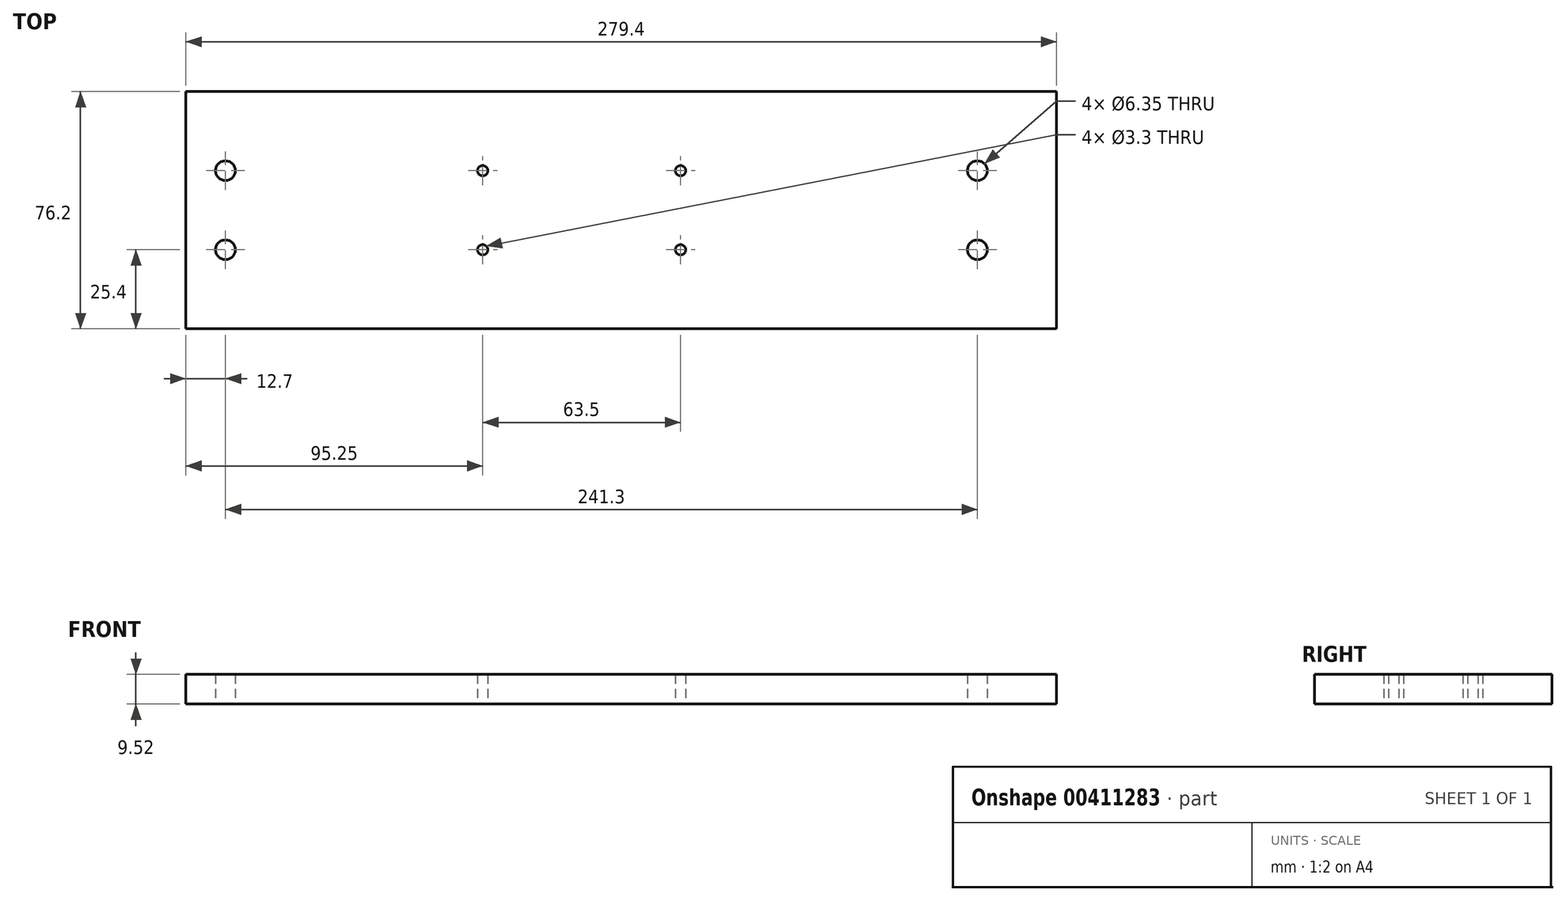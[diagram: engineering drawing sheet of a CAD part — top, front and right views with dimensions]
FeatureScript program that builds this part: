
annotation { "Feature Type Name" : "Feature", "Feature Type Description" : "" }
export const myFeature = defineFeature(function(context is Context, id is Id, definition is map)
    precondition{}
    {
        {
            var Q0;
            Q0=qCreatedBy(makeId("Top.planeOp"),FACE);
            var sketch = newSketch(context, id + "F0", { "sketchPlane" : qUnion([Q0])});
            skLineSegment(sketch, "E0.bottom", {"start": v(-152.4, 38.1) * mm, "end": v(127, 38.1) * mm});
            skLineSegment(sketch, "E0.top", {"start": v(-152.4, -38.1) * mm, "end": v(127, -38.1) * mm});
            skLineSegment(sketch, "E0.left", {"start": v(-152.4, 38.1) * mm, "end": v(-152.4, -38.1) * mm});
            skLineSegment(sketch, "E0.right", {"start": v(127, 38.1) * mm, "end": v(127, -38.1) * mm});
            skCircle(sketch, "E1", {"center": v(-139.7, 12.7) * mm, "radius": 3.18 * mm});
            skCircle(sketch, "E2", {"center": v(-57.15, 12.7) * mm, "radius": 1.65 * mm});
            skCircle(sketch, "E3", {"center": v(6.35, 12.7) * mm, "radius": 1.65 * mm});
            skCircle(sketch, "E4", {"center": v(101.6, 12.7) * mm, "radius": 3.18 * mm});
            skCircle(sketch, "E5.MirrorC", {"center": v(-139.7, -12.7) * mm, "radius": 3.18 * mm});
            skCircle(sketch, "E6.MirrorC", {"center": v(-57.15, -12.7) * mm, "radius": 1.65 * mm});
            skCircle(sketch, "E7.MirrorC", {"center": v(6.35, -12.7) * mm, "radius": 1.65 * mm});
            skCircle(sketch, "E8.MirrorC", {"center": v(101.6, -12.7) * mm, "radius": 3.18 * mm});
            skSolve(sketch);
        }
        {
            var Q0;
            Q0=makeQuery(id+"F0.imprint","IMPRINT",FACE,{"disambiguationData":[TD([[makeQuery(id+"F0.imprint","IMPRINT",EDGE,{"derivedFrom":sQuery(id+"F0.wireOp",EDGE,"E0.bottom")}),-1.0]])]});
            extrude(context, id + "F1", {"entities" : qUnion([Q0]), "endBound" : BoundingType.SYMMETRIC, "depth" : 9.52 * mm});
        }
    });
